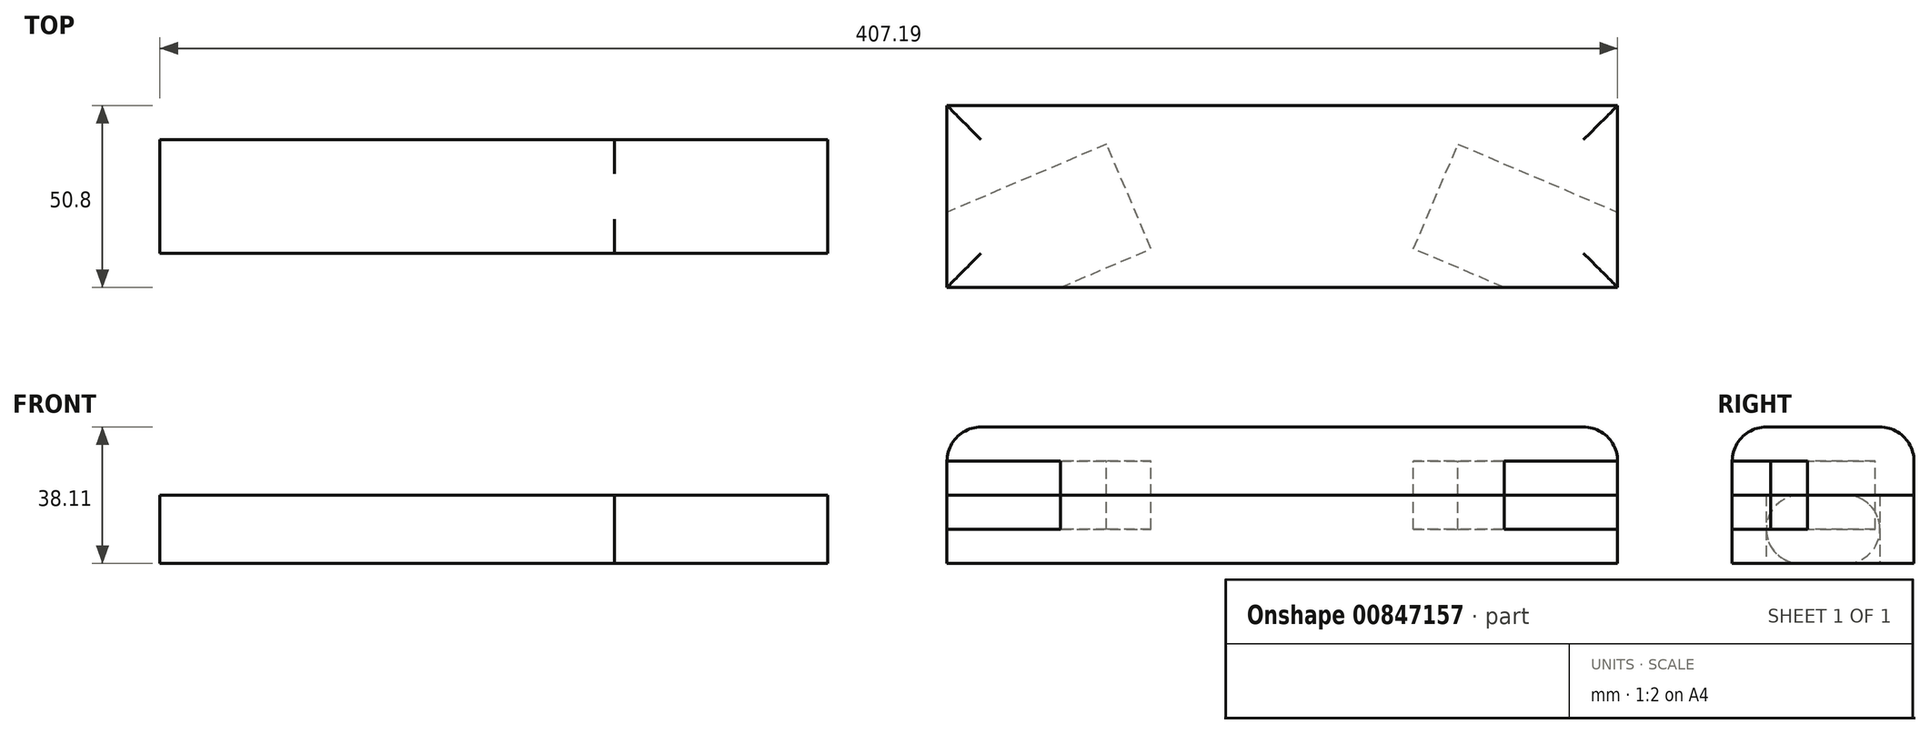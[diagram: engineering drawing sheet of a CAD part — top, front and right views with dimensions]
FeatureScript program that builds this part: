
annotation { "Feature Type Name" : "Feature", "Feature Type Description" : "" }
export const myFeature = defineFeature(function(context is Context, id is Id, definition is map)
    precondition{}
    {
        {
            var Q0;
            Q0=qCreatedBy(makeId("Top.planeOp"),FACE);
            var sketch = newSketch(context, id + "F0", { "sketchPlane" : qUnion([Q0])});
            skLineSegment(sketch, "E0.bottom", {"start": v(93.66, -25.4) * mm, "end": v(-93.66, -25.4) * mm});
            skLineSegment(sketch, "E0.top", {"start": v(93.66, 25.4) * mm, "end": v(-93.66, 25.4) * mm});
            skLineSegment(sketch, "E0.left", {"start": v(93.66, -25.4) * mm, "end": v(93.66, 25.4) * mm});
            skLineSegment(sketch, "E0.right", {"start": v(-93.66, -25.4) * mm, "end": v(-93.66, 25.4) * mm});
            skPoint(sketch, "E0.middle", {"position": v(0, 0) * mm});
            skSolve(sketch);
        }
        {
            var Q0;
            Q0 = qSketchRegion(id + "F0", true);
            extrude(context, id + "F1", {"entities" : qUnion([Q0]), "endBound" : BoundingType.SYMMETRIC, "depth" : 19.05 * mm, "offsetDistance" : 25.4 * mm});
        }
        {
            var Q0;
            Q0=makeQuery(id+"F1.opExtrude","SWEPT_BODY",BODY,{"disambiguationData":[OSD([sQuery(id+"F0.wireOp",EDGE,"E0.bottom"),sQuery(id+"F0.wireOp",EDGE,"E0.top"),sQuery(id+"F0.wireOp",EDGE,"E0.left"),sQuery(id+"F0.wireOp",EDGE,"E0.right")])]});
            transform(context, id + "F2", {"entities" : qUnion([Q0]), "transformType" : TransformType.TRANSLATION_3D, "dx" : 0 * mm, "dy" : 0 * mm, "dz" : 19.05 * mm, "makeCopy" : true});
        }
        {
            var Q0;
            Q0=makeQuery(id+"F2.opPattern","COPY",FACE,{"derivedFrom":makeQuery(id+"F1.opExtrude","CAP_FACE",FACE,{"disambiguationData":[OSD([sQuery(id+"F0.wireOp",EDGE,"E0.bottom"),sQuery(id+"F0.wireOp",EDGE,"E0.top"),sQuery(id+"F0.wireOp",EDGE,"E0.left"),sQuery(id+"F0.wireOp",EDGE,"E0.right")])],"isStart":false}),"instanceName":"1"});
            fillet(context, id + "F3", {"entities" : qUnion([Q0]), "radius" : 9.52 * mm, "tangentPropagation" : true, "allowEdgeOverflow" : false});
        }
        {
            var Q0;
            Q0=qCreatedBy(makeId("Top.planeOp"),FACE);
            var sketch = newSketch(context, id + "F4", { "sketchPlane" : qUnion([Q0])});
            skLineSegment(sketch, "E1.bottom", {"start": v(-127, -15.88) * mm, "end": v(-313.53, -15.88) * mm});
            skLineSegment(sketch, "E1.top", {"start": v(-127, 15.87) * mm, "end": v(-313.53, 15.87) * mm});
            skLineSegment(sketch, "E1.left", {"start": v(-127, -15.88) * mm, "end": v(-127, 15.87) * mm});
            skLineSegment(sketch, "E1.right", {"start": v(-313.53, -15.88) * mm, "end": v(-313.53, 15.87) * mm});
            skPoint(sketch, "E1.middle", {"position": v(-220.27, 0) * mm});
            skSolve(sketch);
        }
        {
            var Q0;
            Q0 = qSketchRegion(id + "F4", true);
            extrude(context, id + "F5", {"entities" : qUnion([Q0]), "endBound" : BoundingType.SYMMETRIC, "depth" : 19.05 * mm, "offsetDistance" : 25.4 * mm});
        }
        {
            var Q0;
            Q0=makeQuery(id+"F5.opExtrude","SWEPT_FACE",FACE,{"disambiguationData":[OSD([sQuery(id+"F4.wireOp",EDGE,"E1.right")])]});
            var sketch = newSketch(context, id + "F6", { "sketchPlane" : qUnion([Q0])});
            skLineSegment(sketch, "E2.left", {"start": v(-15.87, 0) * mm, "end": v(-15.87, 0) * mm});
            skLineSegment(sketch, "E2.right", {"start": v(15.88, 0) * mm, "end": v(15.88, 0) * mm});
            skPoint(sketch, "E3.visualSharp", {"position": v(-15.87, 9.53) * mm});
            skArc(sketch, "E3.filletArc", {"start": v(-6.35, 9.53) * mm, "mid": v(-13.09, 6.74) * mm, "end": v(-15.87, 0) * mm});
            skPoint(sketch, "E4.visualSharp", {"position": v(15.88, 9.53) * mm});
            skArc(sketch, "E4.filletArc", {"start": v(15.88, 0) * mm, "mid": v(13.09, 6.74) * mm, "end": v(6.35, 9.53) * mm});
            skPoint(sketch, "E5.visualSharp", {"position": v(15.88, -9.53) * mm});
            skArc(sketch, "E5.filletArc", {"start": v(6.35, -9.53) * mm, "mid": v(13.09, -6.74) * mm, "end": v(15.88, 0) * mm});
            skPoint(sketch, "E6.visualSharp", {"position": v(-15.87, -9.53) * mm});
            skLineSegment(sketch, "E7", {"start": v(-6.35, 9.53) * mm, "end": v(-15.87, 9.53) * mm});
            skLineSegment(sketch, "E8", {"start": v(-15.87, 0) * mm, "end": v(-15.87, -9.53) * mm});
            skLineSegment(sketch, "E9", {"start": v(6.35, -9.53) * mm, "end": v(15.88, -9.53) * mm});
            skLineSegment(sketch, "E10", {"start": v(15.88, 0) * mm, "end": v(15.88, -9.53) * mm});
            skLineSegment(sketch, "E11", {"start": v(6.35, 9.53) * mm, "end": v(15.88, 9.53) * mm});
            skLineSegment(sketch, "E12", {"start": v(15.88, 9.53) * mm, "end": v(15.88, 0) * mm});
            skLineSegment(sketch, "E13", {"start": v(-15.87, 0) * mm, "end": v(-15.87, 9.53) * mm});
            skLineSegment(sketch, "E14.MirrorCS", {"start": v(-6.35, -9.53) * mm, "end": v(-15.88, -9.53) * mm});
            skLineSegment(sketch, "E15.MirrorCS", {"start": v(-15.88, 0) * mm, "end": v(-15.88, -9.53) * mm});
            skArc(sketch, "E16.MirrorCS", {"start": v(-6.35, -9.53) * mm, "mid": v(-13.09, -6.74) * mm, "end": v(-15.88, 0) * mm});
            skSolve(sketch);
        }
        {
            var Q0;
            Q0 = qSketchRegion(id + "F6", true);
            extrude(context, id + "F7", {"entities" : qUnion([Q0]), "operationType" : NewBodyOperationType.REMOVE, "oppositeDirection" : true, "depth" : 127 * mm, "offsetDistance" : 25.4 * mm});
        }
        {
            var Q0;
            Q0=makeQuery(id+"F1.opExtrude","CAP_FACE",FACE,{"disambiguationData":[OSD([sQuery(id+"F0.wireOp",EDGE,"E0.bottom"),sQuery(id+"F0.wireOp",EDGE,"E0.top"),sQuery(id+"F0.wireOp",EDGE,"E0.left"),sQuery(id+"F0.wireOp",EDGE,"E0.right")])],"isStart":false});
            var sketch = newSketch(context, id + "F8", { "sketchPlane" : qUnion([Q0])});
            skLineSegment(sketch, "E17", {"start": v(-215.9, -73.8) * mm, "end": v(-42.86, 0) * mm, "construction": true});
            skLineSegment(sketch, "E18", {"start": v(42.86, 0) * mm, "end": v(215.9, -73.8) * mm, "construction": true});
            skLineSegment(sketch, "E19.0", {"start": v(-49.1, 14.6) * mm, "end": v(-93.66, -4.4) * mm, "construction": true});
            skLineSegment(sketch, "E20.0", {"start": v(-36.63, -14.6) * mm, "end": v(-61.95, -25.4) * mm, "construction": true});
            skLineSegment(sketch, "E21.0", {"start": v(36.63, -14.6) * mm, "end": v(61.95, -25.4) * mm, "construction": true});
            skLineSegment(sketch, "E22.0", {"start": v(49.1, 14.6) * mm, "end": v(93.66, -4.4) * mm, "construction": true});
            skLineSegment(sketch, "E23", {"start": v(-49.1, 14.6) * mm, "end": v(-36.63, -14.6) * mm, "construction": true});
            skLineSegment(sketch, "E24", {"start": v(49.1, 14.6) * mm, "end": v(36.63, -14.6) * mm, "construction": true});
            skLineSegment(sketch, "E25", {"start": v(0, 25.4) * mm, "end": v(0, -25.4) * mm, "construction": true});
            skLineSegment(sketch, "E26", {"start": v(-93.66, -4.4) * mm, "end": v(-93.66, -38.93) * mm, "construction": true});
            skLineSegment(sketch, "E27", {"start": v(-93.66, -38.93) * mm, "end": v(-36.63, -14.6) * mm, "construction": true});
            skLineSegment(sketch, "E28", {"start": v(36.63, -14.6) * mm, "end": v(93.66, -38.93) * mm, "construction": true});
            skLineSegment(sketch, "E29", {"start": v(93.66, -38.93) * mm, "end": v(93.66, -4.4) * mm, "construction": true});
            skLineSegment(sketch, "E30", {"start": v(-93.66, -4.4) * mm, "end": v(-93.66, -25.4) * mm, "construction": true});
            skLineSegment(sketch, "E31", {"start": v(-93.66, -25.4) * mm, "end": v(-61.95, -25.4) * mm, "construction": true});
            skLineSegment(sketch, "E32", {"start": v(93.66, -25.4) * mm, "end": v(93.66, -4.4) * mm, "construction": true});
            skLineSegment(sketch, "E33", {"start": v(-61.95, -25.4) * mm, "end": v(-36.63, -14.6) * mm, "construction": true});
            skLineSegment(sketch, "E34", {"start": v(61.95, -25.4) * mm, "end": v(93.66, -25.4) * mm, "construction": true});
            skLineSegment(sketch, "E35", {"start": v(-93.66, -25.4) * mm, "end": v(-61.95, -25.4) * mm});
            skLineSegment(sketch, "E36", {"start": v(-61.95, -25.4) * mm, "end": v(-36.63, -14.6) * mm});
            skLineSegment(sketch, "E37", {"start": v(-36.63, -14.6) * mm, "end": v(-49.1, 14.6) * mm});
            skLineSegment(sketch, "E38", {"start": v(-49.1, 14.6) * mm, "end": v(-93.66, -4.4) * mm});
            skLineSegment(sketch, "E39", {"start": v(-93.66, -4.4) * mm, "end": v(-93.66, -25.4) * mm});
            skLineSegment(sketch, "E40", {"start": v(36.63, -14.6) * mm, "end": v(49.1, 14.6) * mm});
            skLineSegment(sketch, "E41", {"start": v(49.1, 14.6) * mm, "end": v(93.66, -4.4) * mm});
            skLineSegment(sketch, "E42", {"start": v(93.66, -4.4) * mm, "end": v(93.66, -25.4) * mm});
            skLineSegment(sketch, "E43", {"start": v(93.66, -25.4) * mm, "end": v(61.95, -25.4) * mm});
            skLineSegment(sketch, "E44", {"start": v(61.95, -25.4) * mm, "end": v(36.63, -14.6) * mm});
            skSolve(sketch);
        }
        {
            var Q0;
            Q0 = qSketchRegion(id + "F8", true);
            extrude(context, id + "F9", {"entities" : qUnion([Q0]), "operationType" : NewBodyOperationType.REMOVE, "endBound" : BoundingType.SYMMETRIC, "oppositeDirection" : true, "depth" : 19.05 * mm, "offsetDistance" : 25.4 * mm});
        }
    });
